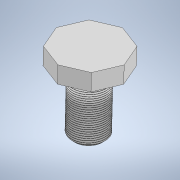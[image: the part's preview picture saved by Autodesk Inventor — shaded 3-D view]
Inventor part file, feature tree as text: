
AUTODESK INVENTOR PART (.ipt)
format: ipt  version: 2021 (Build 250183000, 183)  size: 1,166,848 bytes
history: native  units: in
note: dims shown in document units (in); Inventor stores cm internally (conversion verified against a paired STEP export)
features: other x4, sketch x4, extrude x3, plane x2, chamfer x1, helix x1
ambient origin geometry x8: Origin, YZ Plane, XZ Plane, XY Plane, X Axis, Y Axis, Z Axis, Center Point
bodies: Solid1 (feature_tree)
feature tree (15):
  plane  "Work Plane3"
  extrude  "Extrusion1"  Depth=2.126in TaperAngle=0.0deg
  extrude  "Extrusion2"  Depth=0.5906in TaperAngle=0.0deg
  chamfer  "Chamfer1"  Distance=0.1181in Angle=45.0deg
  other  "Work Axis1"
  extrude  "Extrusion3"  Depth=0.5906in TaperAngle=360.0deg
  plane  "Work Plane5"
  helix  "Coil2"  [1 undecoded]
  sketch  "Sketch3"  dims[d0=1.1811in d1=2.126in d2=0.0in]
  sketch  "Sketch4"  dims[d3=2.3622in d4=0.5906in d5=0.0in d8=0.1181in d9=0.0787in d10=45.0deg]
  sketch  "Sketch7"  dims[d27=45.0deg d28=3.1496in d30=360.0deg d32=0.5906in d33=0.0in]
  sketch  "Sketch8"  dims[d34=90.0deg d35=0.0787in d36=0.0295in d37=0.0079in d38=0.1181in d39=0.0669in d40=2.2343in d41=0.3937in d42=0.0in d43=90.0deg d44=90.0deg d45=0.0in d46=0.0in]
  parser-record x1  (decoder bookkeeping rows leaked as tree rows — omitted from the tree; the rows remain in map.json)
  other  "Pen_Plotter.iam"
  other  "Clamp_Main_Body:1"
note: 1 required parameter value undecoded (feature->parameter linkage not recoverable at this tier; creation-order binding heuristic only, values carry confidence <= 0.55)
note: 1 file-system path scrubbed to <path> (originals preserved in map.json)
